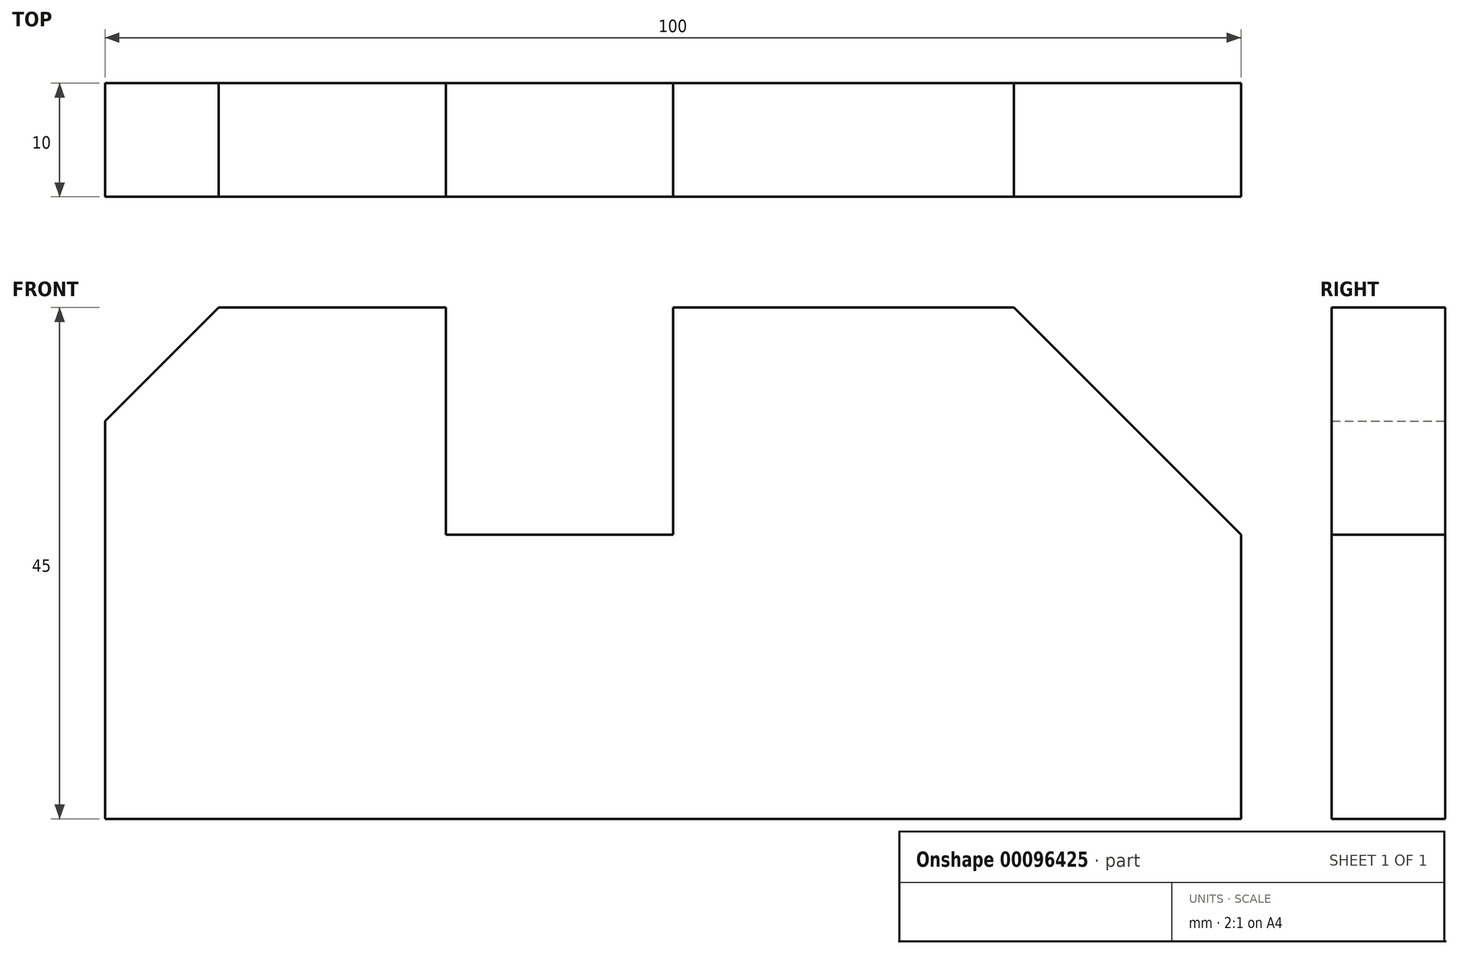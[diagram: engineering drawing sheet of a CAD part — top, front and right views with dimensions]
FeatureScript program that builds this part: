
annotation { "Feature Type Name" : "Feature", "Feature Type Description" : "" }
export const myFeature = defineFeature(function(context is Context, id is Id, definition is map)
    precondition{}
    {
        {
            var Q0;
            Q0=qCreatedBy(makeId("Front.planeOp"),FACE);
            var sketch = newSketch(context, id + "F0", { "sketchPlane" : qUnion([Q0])});
            skLineSegment(sketch, "E0.bottom", {"start": v(0, 0) * mm, "end": v(100, 0) * mm, "construction": true});
            skLineSegment(sketch, "E0.top", {"start": v(0, 45) * mm, "end": v(100, 45) * mm, "construction": true});
            skLineSegment(sketch, "E0.left", {"start": v(0, 0) * mm, "end": v(0, 45) * mm, "construction": true});
            skLineSegment(sketch, "E0.right", {"start": v(100, 0) * mm, "end": v(100, 45) * mm, "construction": true});
            skLineSegment(sketch, "E1", {"start": v(0, 0) * mm, "end": v(100, 0) * mm});
            skLineSegment(sketch, "E2", {"start": v(0, 0) * mm, "end": v(0, 35) * mm});
            skLineSegment(sketch, "E3", {"start": v(0, 35) * mm, "end": v(10, 45) * mm});
            skLineSegment(sketch, "E4", {"start": v(10, 45) * mm, "end": v(30, 45) * mm});
            skLineSegment(sketch, "E5", {"start": v(30, 45) * mm, "end": v(30, 25) * mm});
            skLineSegment(sketch, "E6", {"start": v(30, 25) * mm, "end": v(50, 25) * mm});
            skLineSegment(sketch, "E7", {"start": v(50, 25) * mm, "end": v(50, 45) * mm});
            skLineSegment(sketch, "E8", {"start": v(50, 45) * mm, "end": v(80, 45) * mm});
            skLineSegment(sketch, "E9", {"start": v(80, 45) * mm, "end": v(100, 25) * mm});
            skLineSegment(sketch, "E10", {"start": v(100, 25) * mm, "end": v(100, 0) * mm});
            skSolve(sketch);
        }
        {
            var Q0;
            Q0 = qSketchRegion(id + "F0", true);
            extrude(context, id + "F1", {"entities" : qUnion([Q0]), "endBound" : BoundingType.SYMMETRIC, "depth" : 10 * mm});
        }
    });
